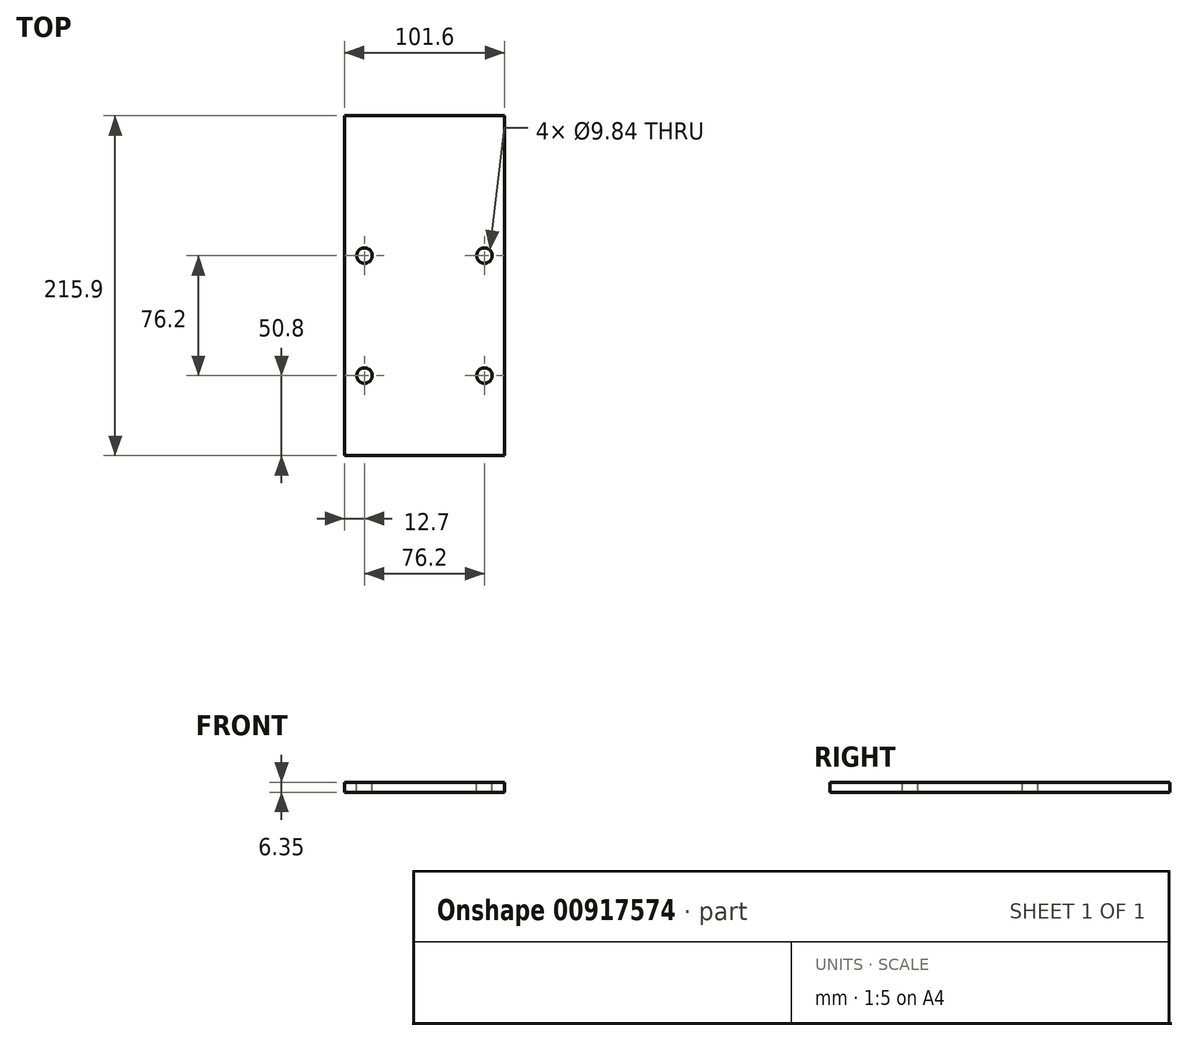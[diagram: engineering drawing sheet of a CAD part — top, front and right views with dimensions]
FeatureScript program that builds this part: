
annotation { "Feature Type Name" : "Feature", "Feature Type Description" : "" }
export const myFeature = defineFeature(function(context is Context, id is Id, definition is map)
    precondition{}
    {
        {
            var Q0;
            Q0=qCreatedBy(makeId("Top.planeOp"),FACE);
            var sketch = newSketch(context, id + "F0", { "sketchPlane" : qUnion([Q0])});
            skLineSegment(sketch, "E0.bottom", {"start": v(0, 0) * mm, "end": v(101.6, 0) * mm});
            skLineSegment(sketch, "E0.top", {"start": v(0, 215.9) * mm, "end": v(101.6, 215.9) * mm});
            skLineSegment(sketch, "E0.left", {"start": v(0, 0) * mm, "end": v(0, 215.9) * mm});
            skLineSegment(sketch, "E0.right", {"start": v(101.6, 0) * mm, "end": v(101.6, 215.9) * mm});
            skSolve(sketch);
        }
        {
            var Q0;
            Q0=makeQuery(id+"F0.imprint","IMPRINT",FACE,{"disambiguationData":[TD([[makeQuery(id+"F0.imprint","IMPRINT",EDGE,{"derivedFrom":sQuery(id+"F0.wireOp",EDGE,"E0.bottom")}),1.0]])]});
            extrude(context, id + "F1", {"entities" : qUnion([Q0]), "depth" : 6.35 * mm, "offsetDistance" : 25.4 * mm});
        }
        {
            var Q0;
            Q0=makeQuery(id+"F1.opExtrude","CAP_FACE",FACE,{"disambiguationData":[OSD([sQuery(id+"F0.wireOp",EDGE,"E0.bottom"),sQuery(id+"F0.wireOp",EDGE,"E0.top"),sQuery(id+"F0.wireOp",EDGE,"E0.left"),sQuery(id+"F0.wireOp",EDGE,"E0.right")])],"isStart":false});
            var sketch = newSketch(context, id + "F2", { "sketchPlane" : qUnion([Q0])});
            skLineSegment(sketch, "E1.bottom", {"start": v(12.7, 50.8) * mm, "end": v(88.9, 50.8) * mm});
            skLineSegment(sketch, "E1.top", {"start": v(12.7, 127) * mm, "end": v(88.9, 127) * mm});
            skLineSegment(sketch, "E1.left", {"start": v(12.7, 50.8) * mm, "end": v(12.7, 127) * mm});
            skLineSegment(sketch, "E1.right", {"start": v(88.9, 50.8) * mm, "end": v(88.9, 127) * mm});
            skSolve(sketch);
        }
        {
            var Q0;
            Q0=sQuery(id+"F2.wireOp",VERTEX,"E1.top.start");
            var Q1;
            Q1=sQuery(id+"F2.wireOp",VERTEX,"E1.top.end");
            var Q2;
            Q2=sQuery(id+"F2.wireOp",VERTEX,"E1.bottom.end");
            var Q3;
            Q3=sQuery(id+"F2.wireOp",VERTEX,"E1.bottom.start");
            var Q4;
            Q4=makeQuery(id+"F1.opExtrude","SWEPT_BODY",BODY,{"disambiguationData":[OSD([sQuery(id+"F0.wireOp",EDGE,"E0.bottom"),sQuery(id+"F0.wireOp",EDGE,"E0.top"),sQuery(id+"F0.wireOp",EDGE,"E0.left"),sQuery(id+"F0.wireOp",EDGE,"E0.right")])]});
            hole(context, id + "F3", {"style" : HoleStyle.SIMPLE, "endStyle" : HoleEndStyle.THROUGH, "holeDiameter" : 9.84 * mm, "majorDiameter" : 6.35 * mm, "isTappedThrough" : true, "tappedDepth" : 12.7 * mm, "tapClearance" : 3, "locations" : qUnion([Q0, Q1, Q2, Q3]), "scope" : qUnion([Q4])});
        }
    });
